# Revit family: Parex_SpecialityEquipment_Emma_Rangehood
name_source: partatom
category: Specialty Equipment
units: mm (PartAtom-declared; Revit-internal decimal feet)

## family parameters
Always vertical = Yes
Cut with Voids When Loaded = Yes
Enable Cutting in Views = Yes
Maintain Annotation Orientation = No
Part Type = Normal
Room Calculation Point = No
Round Connector Dimension = Use Diameter
Shared = No
Work Plane-Based = No

## types (1)
- Parex_SpecialityEquipment_Emma_Rangehood
    Calc_FrameOffset = 10 mm  [stored 0.0328084 ft]
    Calc_GrillFrameWidth = 10 mm  [stored 0.0328084 ft]
    Calc_RearFrameWidth = 90 mm
    Calc_SpotlightDiameter = 85 mm
    Calc_SpotlightInnerDiameter = 75 mm
    Default Elevation = 285 mm
    Depth = 360 mm  [stored 1.1811 ft]
    Description = The Emma 600mm undermount rangehood is suitable for up to a 600mm wide cooktop fitting effortlessly into your kitchen cabinetry and can be matched with a motor tailored to your cooking requirements.
    Export Type to IFC As = IfcElectricApplianceType
    FilterMaterial = Parex_Metal_Filter
    Height = 285 mm
    HoodThickness = 10 mm  [stored 0.0328084 ft]
    InnerBaseWidth = 564 mm  [stored 1.85039 ft]
    InnerHeight = 285 mm
    InnerTopWidth = 500 mm  [stored 1.64042 ft]
    Manufacturer = Amore Homes
    Material = Parex_Metal_430 Stainless Steel
    Model = Emma 600mm Undermount Rangehood
    MountType = Undermount
    Specifications = Quiet operation with external motor

Expel smoke, grease, smells & steam outside

Easy control with soft touch eye level controls

Great control with 5-speed levels

15-Minute delay timer with auto shut-off

Twin LED lights gives you great stove top lighting

Sturdy hood made of 1mm 430 stainless steel

Stainless steel dishwasher safe filters

Remote control for optimum convenience

Includes 5m ducting
    Type IFC Predefined Type = NOTDEFINED
    URL = https://amorehomes.co.nz
    WarrantyDescription = 5-Year in-home warranty on hood, 10-Year in-home warranty on motor
    Width = 600 mm

note: [stored X ft] marks values corroborated as IEEE doubles in the binary element streams (Revit-internal decimal feet)

## geometry (parser evidence)
native form markers: Sweep x7
no freeform markers — native parametric forms only
